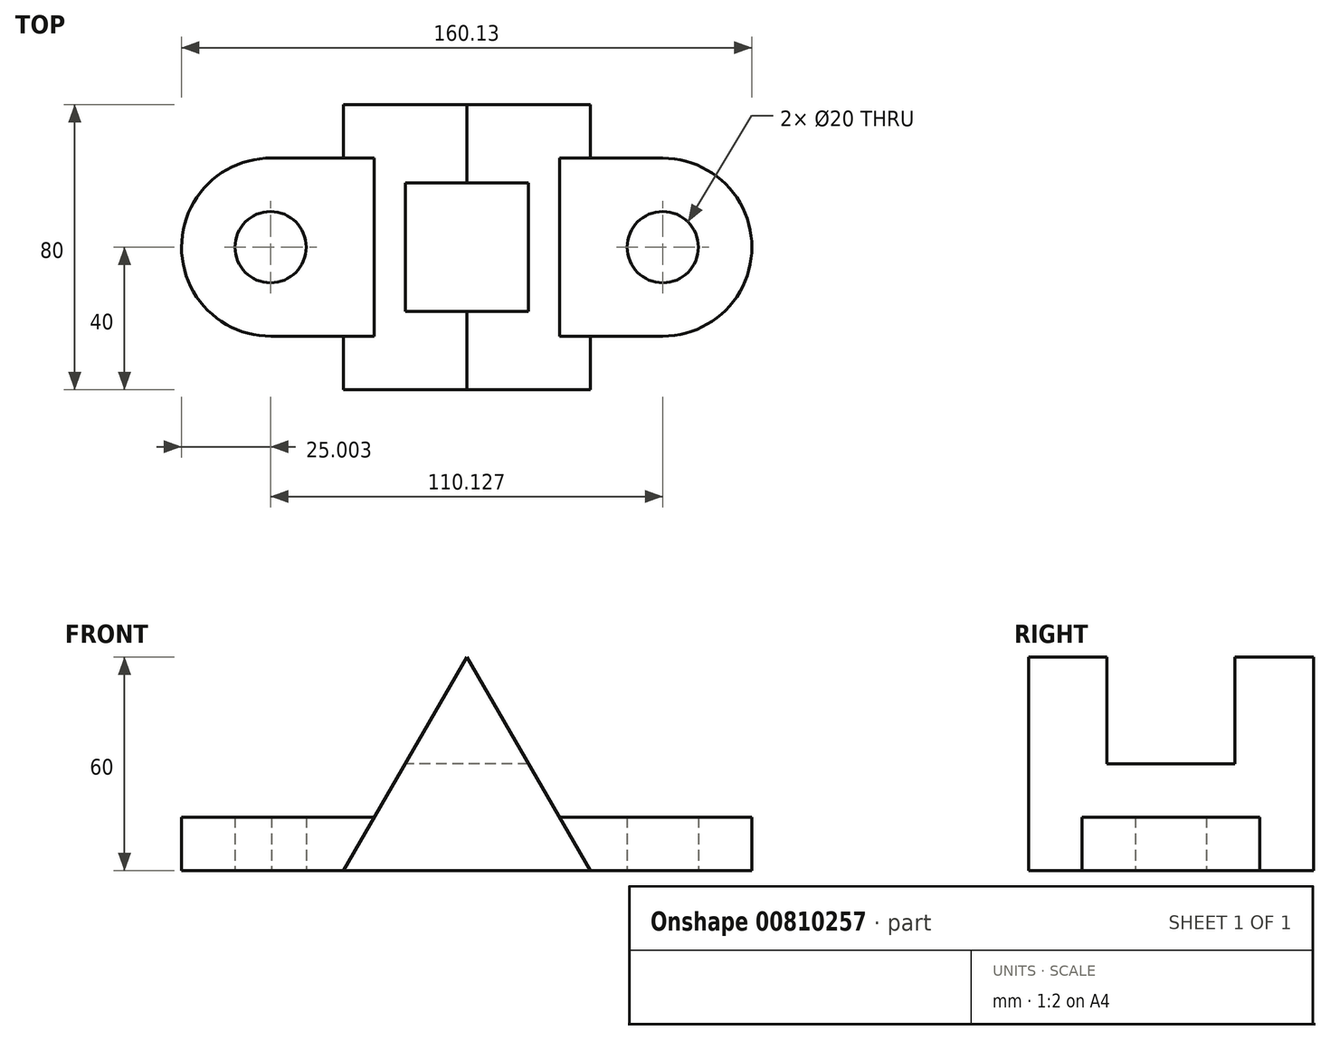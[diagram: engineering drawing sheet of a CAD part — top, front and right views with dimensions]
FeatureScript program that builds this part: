
annotation { "Feature Type Name" : "Feature", "Feature Type Description" : "" }
export const myFeature = defineFeature(function(context is Context, id is Id, definition is map)
    precondition{}
    {
        {
            var Q0;
            Q0=qCreatedBy(makeId("Top.planeOp"),FACE);
            var sketch = newSketch(context, id + "F0", { "sketchPlane" : qUnion([Q0])});
            skCircle(sketch, "E0", {"center": v(-42.93, 0) * mm, "radius": 10 * mm});
            skCircle(sketch, "E1", {"center": v(67.2, 0) * mm, "radius": 10 * mm});
            skCircle(sketch, "E2", {"center": v(-42.93, 0) * mm, "radius": 25 * mm});
            skCircle(sketch, "E3", {"center": v(67.2, 0) * mm, "radius": 25 * mm});
            skLineSegment(sketch, "E4", {"start": v(68.21, 25) * mm, "end": v(68.21, 25) * mm});
            skLineSegment(sketch, "E5", {"start": v(-42.8, -25) * mm, "end": v(67.2, -25) * mm});
            skLineSegment(sketch, "E6", {"start": v(-42.67, 25) * mm, "end": v(68.21, 25) * mm});
            skSolve(sketch);
        }
        {
            var Q0;
            Q0=makeQuery(id+"F0.imprint","IMPRINT",FACE,{"disambiguationData":[TD([[makeQuery(id+"F0.imprint","IMPRINT",EDGE,{"derivedFrom":sQuery(id+"F0.wireOp",EDGE,"E0")}),-1.0]])]});
            var Q1;
            Q1=makeQuery(id+"F0.imprint","IMPRINT",FACE,{"disambiguationData":[TD([[makeQuery(id+"F0.imprint","IMPRINT",EDGE,{"derivedFrom":sQuery(id+"F0.wireOp",EDGE,"E1")}),-1.0]])]});
            extrude(context, id + "F1", {"entities" : qUnion([Q0, Q1]), "depth" : 15 * mm, "offsetDistance" : 25 * mm});
        }
        {
            var Q0;
            {var subQ5=sQuery(id+"F0.wireOp",EDGE,"E6");Q0=makeQuery(id+"F0.imprint","IMPRINT",FACE,{"disambiguationData":[TD([[makeQuery(id+"F0.imprint","IMPRINT",EDGE,{"derivedFrom":subQ5}),-1.0]])]});}
            var Q1;
            Q1=makeQuery(id+"F0.imprint","IMPRINT",FACE,{"disambiguationData":[TD([[makeQuery(id+"F0.imprint","IMPRINT",EDGE,{"derivedFrom":sQuery(id+"F0.wireOp",EDGE,"E0")}),-1.0]])]});
            var Q2;
            {var subQ0=sQuery(id+"F0.wireOp",EDGE,"UDObbfMg-nirE-b7m0-81qE-yLwgkopyre70");var subQ3=sQuery(id+"F0.wireOp",EDGE,"E1");var subQ4=makeQuery(id+"F0.imprint","INTERSECT",VERTEX,{"disambiguationData":[OD(0.0)],"derivedFrom":[subQ3,subQ0]});Q2=makeQuery(id+"F0.imprint","IMPRINT",FACE,{"disambiguationData":[TD([[makeQuery(id+"F0.imprint","IMPRINT",EDGE,{"disambiguationData":[TD([[subQ4,-1.0]])],"derivedFrom":subQ3}),-1.0]])]});}
            var Q3;
            {var subQ0=sQuery(id+"F0.wireOp",EDGE,"UDObbfMg-nirE-b7m0-81qE-yLwgkopyre70");var subQ1=sQuery(id+"F0.wireOp",EDGE,"E1");var subQ2=makeQuery(id+"F0.imprint","INTERSECT",VERTEX,{"disambiguationData":[OD(0.0)],"derivedFrom":[subQ1,subQ0]});Q3=makeQuery(id+"F0.imprint","IMPRINT",FACE,{"disambiguationData":[TD([[makeQuery(id+"F0.imprint","IMPRINT",EDGE,{"disambiguationData":[TD([[subQ2,1.0]])],"derivedFrom":subQ1}),-1.0]])]});}
            extrude(context, id + "F2", {"entities" : qUnion([Q0, Q1, Q2, Q3]), "depth" : 15 * mm, "offsetDistance" : 25 * mm});
        }
        {
            var Q0;
            Q0=qCreatedBy(makeId("Front.planeOp"),FACE);
            var sketch = newSketch(context, id + "F3", { "sketchPlane" : qUnion([Q0])});
            skCircle(sketch, "E7.cCircle", {"center": v(12.2, 20) * mm, "radius": 20 * mm, "construction": true});
            skLineSegment(sketch, "E7.0", {"start": v(46.84, 0) * mm, "end": v(-22.44, 0) * mm});
            skLineSegment(sketch, "E7.1", {"start": v(-22.44, 0) * mm, "end": v(12.2, 60) * mm});
            skLineSegment(sketch, "E7.2", {"start": v(12.2, 60) * mm, "end": v(46.84, 0) * mm});
            skPoint(sketch, "E7.0.midPoint", {"position": v(12.2, 0) * mm});
            skSolve(sketch);
        }
        {
            var Q0;
            Q0 = qSketchRegion(id + "F3", true);
            extrude(context, id + "F4", {"entities" : qUnion([Q0]), "operationType" : NewBodyOperationType.ADD, "depth" : 40 * mm, "offsetDistance" : 25 * mm, "hasSecondDirection" : true, "secondDirectionOppositeDirection" : true, "secondDirectionDepth" : 40 * mm});
        }
        {
            var Q0;
            Q0=qCreatedBy(makeId("Right.planeOp"),FACE);
            var sketch = newSketch(context, id + "F5", { "sketchPlane" : qUnion([Q0])});
            skLineSegment(sketch, "E8.bottom", {"start": v(-18, 60) * mm, "end": v(18, 60) * mm});
            skLineSegment(sketch, "E8.top", {"start": v(-18, 30) * mm, "end": v(18, 30) * mm});
            skLineSegment(sketch, "E8.left", {"start": v(-18, 60) * mm, "end": v(-18, 30) * mm});
            skLineSegment(sketch, "E8.right", {"start": v(18, 60) * mm, "end": v(18, 30) * mm});
            skSolve(sketch);
        }
        {
            var Q0;
            Q0 = qSketchRegion(id + "F5", true);
            extrude(context, id + "F6", {"entities" : qUnion([Q0]), "operationType" : NewBodyOperationType.REMOVE, "depth" : 200 * mm, "offsetDistance" : 25 * mm, "hasSecondDirection" : true, "secondDirectionOppositeDirection" : true, "secondDirectionDepth" : 320 * mm});
        }
    });
